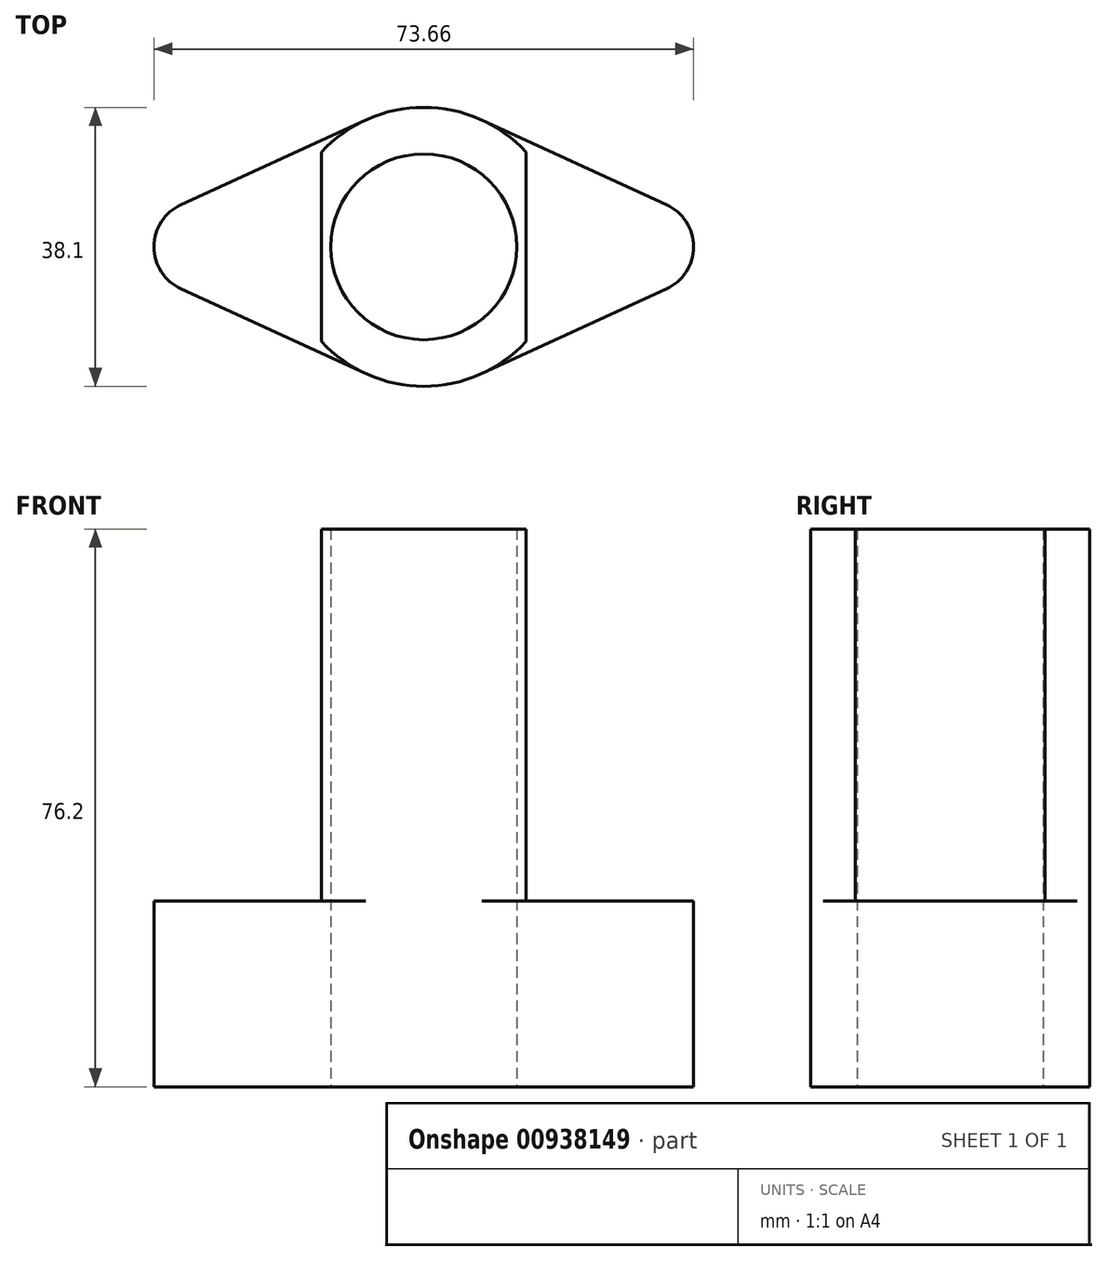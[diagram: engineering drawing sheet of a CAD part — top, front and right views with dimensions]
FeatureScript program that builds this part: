
annotation { "Feature Type Name" : "Feature", "Feature Type Description" : "" }
export const myFeature = defineFeature(function(context is Context, id is Id, definition is map)
    precondition{}
    {
        {
            var Q0;
            Q0=qCreatedBy(makeId("Top.planeOp"),FACE);
            var sketch = newSketch(context, id + "F0", { "sketchPlane" : qUnion([Q0])});
            skArc(sketch, "E0", {"start": v(-7.94, -17.32) * mm, "mid": v(0, -19.05) * mm, "end": v(7.94, -17.32) * mm});
            skArc(sketch, "E1", {"start": v(33.13, -5.77) * mm, "mid": v(36.83, 0) * mm, "end": v(33.13, 5.77) * mm});
            skArc(sketch, "E2", {"start": v(-33.13, 5.77) * mm, "mid": v(-36.83, 0) * mm, "end": v(-33.13, -5.77) * mm});
            skLineSegment(sketch, "E3", {"start": v(33.13, 5.77) * mm, "end": v(7.94, 17.32) * mm});
            skLineSegment(sketch, "E4", {"start": v(33.13, -5.77) * mm, "end": v(7.94, -17.32) * mm});
            skLineSegment(sketch, "E5", {"start": v(-33.13, 5.77) * mm, "end": v(-7.94, 17.32) * mm});
            skLineSegment(sketch, "E6", {"start": v(-33.13, -5.77) * mm, "end": v(-7.94, -17.32) * mm});
            skArc(sketch, "E7.trimOffspring", {"start": v(7.94, 17.32) * mm, "mid": v(0, 19.05) * mm, "end": v(-7.94, 17.32) * mm});
            skCircle(sketch, "E8", {"center": v(0, 0) * mm, "radius": 12.7 * mm});
            skSolve(sketch);
        }
        {
            var Q0;
            Q0 = qSketchRegion(id + "F0", true);
            extrude(context, id + "F1", {"entities" : qUnion([Q0]), "depth" : 25.4 * mm, "offsetDistance" : 25.4 * mm});
        }
        {
            var Q0;
            Q0=makeQuery(id+"F1.opExtrude","CAP_FACE",FACE,{"disambiguationData":[OSD([sQuery(id+"F0.wireOp",EDGE,"E0"),sQuery(id+"F0.wireOp",EDGE,"E1"),sQuery(id+"F0.wireOp",EDGE,"E2"),sQuery(id+"F0.wireOp",EDGE,"E3"),sQuery(id+"F0.wireOp",EDGE,"E4"),sQuery(id+"F0.wireOp",EDGE,"E5"),sQuery(id+"F0.wireOp",EDGE,"E6"),sQuery(id+"F0.wireOp",EDGE,"E7.trimOffspring"),sQuery(id+"F0.wireOp",EDGE,"E8")])],"isStart":false});
            var sketch = newSketch(context, id + "F2", { "sketchPlane" : qUnion([Q0])});
            skArc(sketch, "E9.0", {"start": v(13.97, 12.95) * mm, "mid": v(0, 19.05) * mm, "end": v(-13.97, 12.95) * mm});
            skArc(sketch, "E10.0", {"start": v(-13.97, -12.95) * mm, "mid": v(0, -19.05) * mm, "end": v(13.97, -12.95) * mm});
            skLineSegment(sketch, "E11", {"start": v(13.97, 12.95) * mm, "end": v(13.97, -12.95) * mm});
            skLineSegment(sketch, "E12", {"start": v(0, -32.72) * mm, "end": v(0, 40.65) * mm, "construction": true});
            skPoint(sketch, "E13.orphan", {"position": v(7.94, 17.32) * mm});
            skPoint(sketch, "E14.orphan", {"position": v(7.94, -17.32) * mm});
            skLineSegment(sketch, "E15.MirrorCS", {"start": v(-13.97, 12.95) * mm, "end": v(-13.97, -12.95) * mm});
            skPoint(sketch, "E16.orphan", {"position": v(-7.94, 17.32) * mm});
            skPoint(sketch, "E17.orphan", {"position": v(-7.94, -17.32) * mm});
            skSolve(sketch);
        }
        {
            var Q0;
            {var subQ6=sQuery(id+"F2.wireOp",EDGE,"E11");Q0=makeQuery(id+"F2.imprint","IMPRINT",FACE,{"disambiguationData":[TD([[makeQuery(id+"F2.imprint","IMPRINT",EDGE,{"derivedFrom":subQ6}),-1.0]])]});}
            extrude(context, id + "F3", {"entities" : qUnion([Q0]), "operationType" : NewBodyOperationType.ADD, "depth" : 50.8 * mm, "offsetDistance" : 25.4 * mm});
        }
    });
